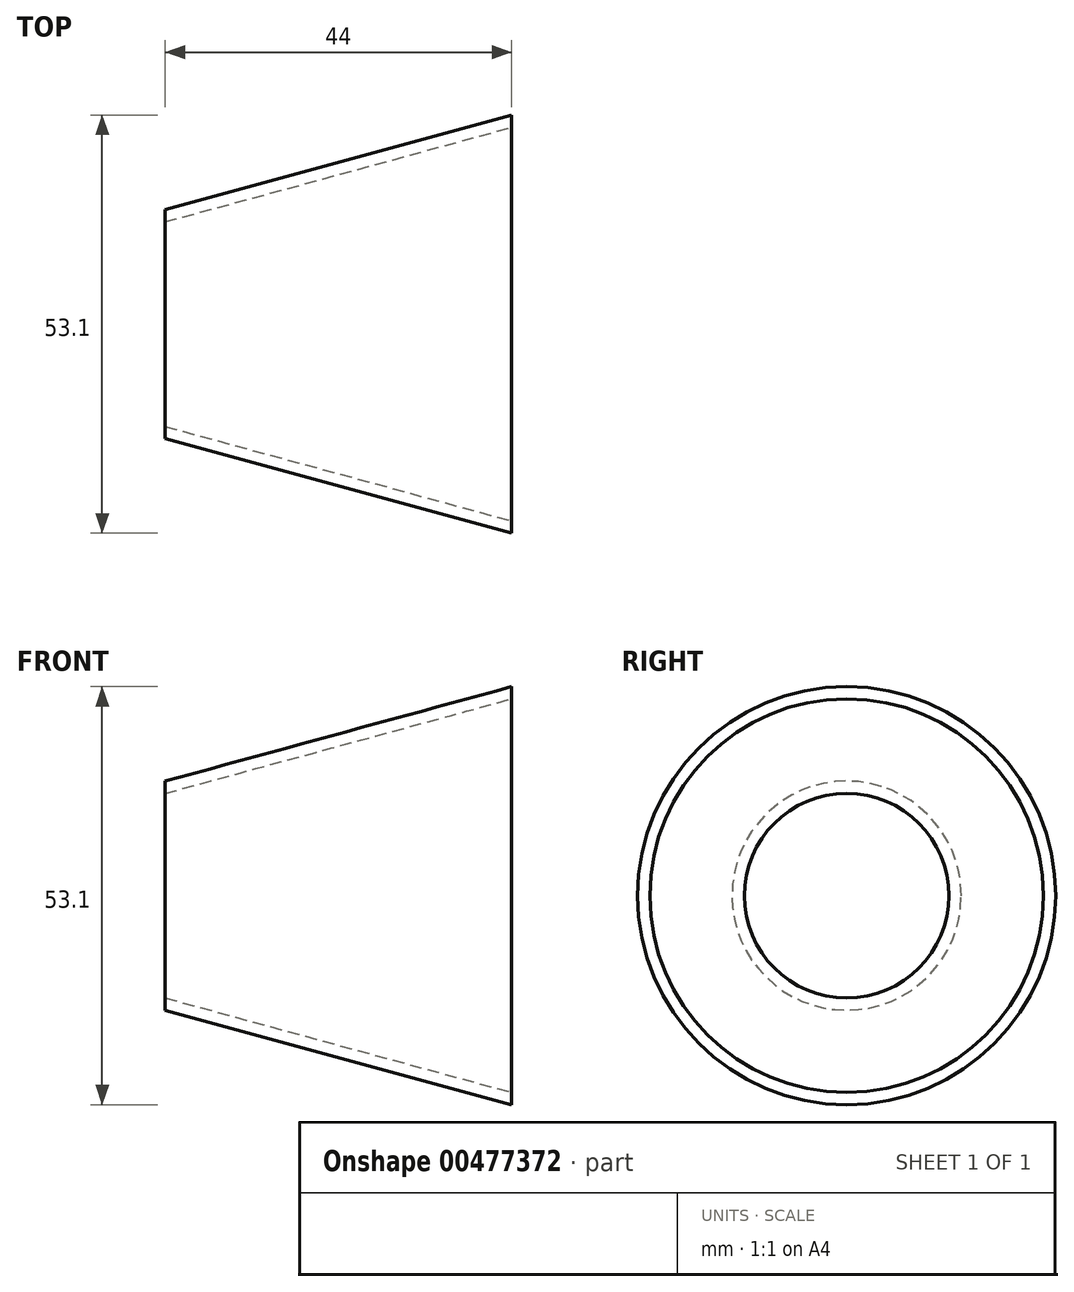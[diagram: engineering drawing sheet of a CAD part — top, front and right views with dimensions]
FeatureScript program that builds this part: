
annotation { "Feature Type Name" : "Feature", "Feature Type Description" : "" }
export const myFeature = defineFeature(function(context is Context, id is Id, definition is map)
    precondition{}
    {
        {
            var Q0;
            Q0=qCreatedBy(makeId("Front.planeOp"),FACE);
            var sketch = newSketch(context, id + "F0", { "sketchPlane" : qUnion([Q0])});
            skLineSegment(sketch, "E0", {"start": v(0, 0) * mm, "end": v(26.48, 0) * mm, "construction": true});
            skLineSegment(sketch, "E1", {"start": v(0, 13) * mm, "end": v(0, 14.55) * mm});
            skLineSegment(sketch, "E2", {"start": v(0, 14.55) * mm, "end": v(44, 26.55) * mm});
            skLineSegment(sketch, "E3", {"start": v(44, 26.55) * mm, "end": v(44, 25) * mm});
            skLineSegment(sketch, "E4", {"start": v(44, 25) * mm, "end": v(0, 13) * mm});
            skSolve(sketch);
        }
        {
            var Q0;
            Q0 = qSketchRegion(id + "F0", true);
            var Q1;
            Q1=sQuery(id+"F0.wireOp",EDGE,"E0");
            revolve(context, id + "F1", {"entities" : qUnion([Q0]), "axis" : qUnion([Q1]), "revolveType" : RevolveType.FULL});
        }
    });
